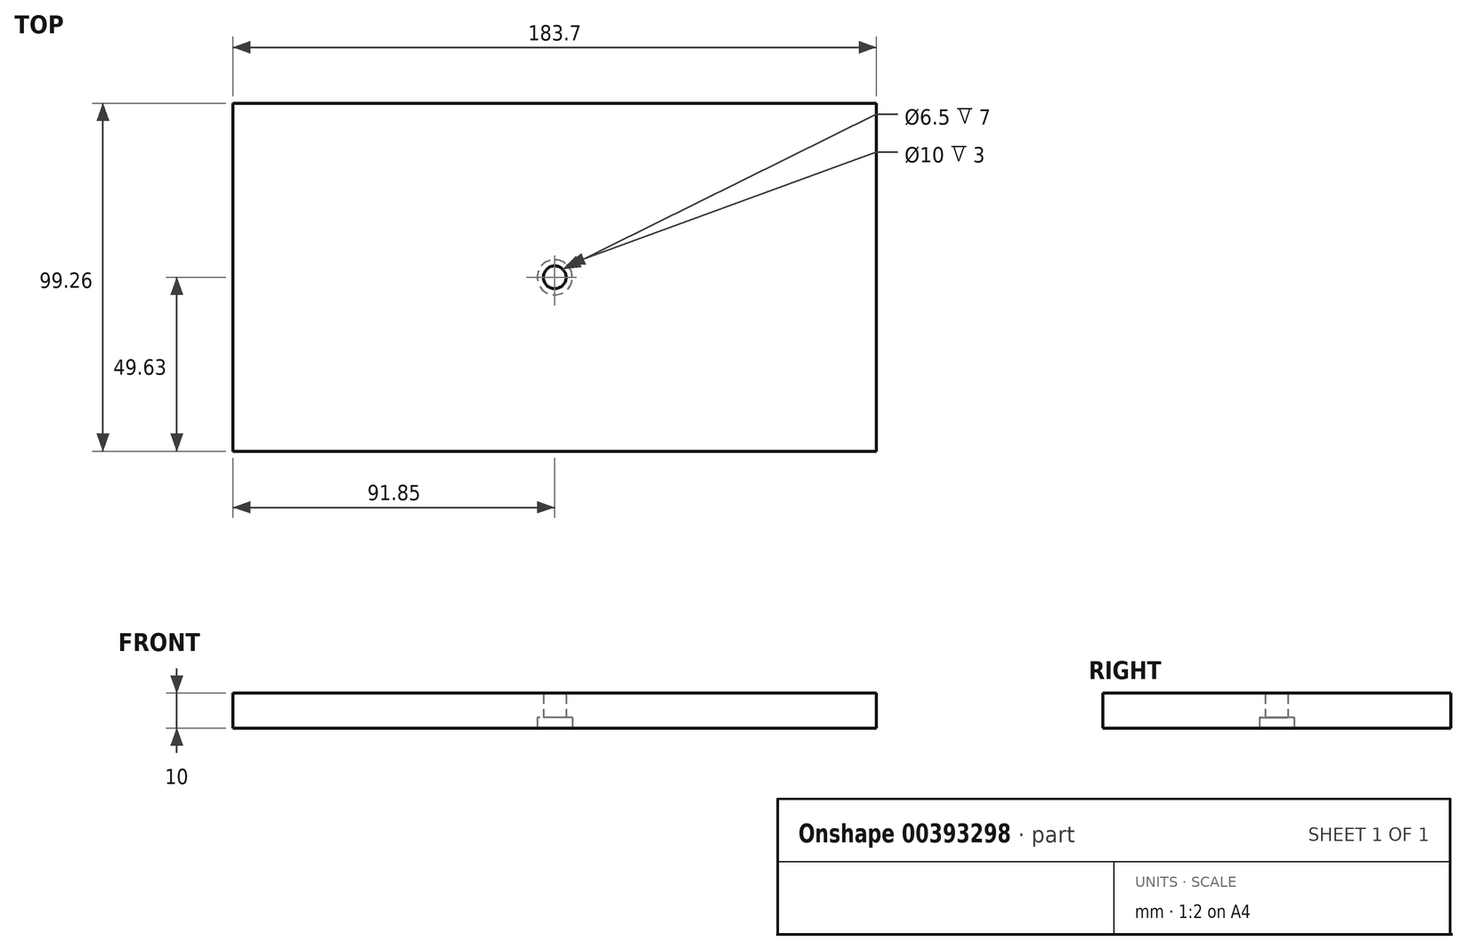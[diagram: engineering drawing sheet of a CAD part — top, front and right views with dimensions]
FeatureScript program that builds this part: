
annotation { "Feature Type Name" : "Feature", "Feature Type Description" : "" }
export const myFeature = defineFeature(function(context is Context, id is Id, definition is map)
    precondition{}
    {
        {
            var Q0;
            Q0=qCreatedBy(makeId("Top.planeOp"),FACE);
            var sketch = newSketch(context, id + "F0", { "sketchPlane" : qUnion([Q0])});
            skLineSegment(sketch, "E0.bottom", {"start": v(-91.85, 49.63) * mm, "end": v(91.85, 49.63) * mm});
            skLineSegment(sketch, "E0.top", {"start": v(-91.85, -49.63) * mm, "end": v(91.85, -49.63) * mm});
            skLineSegment(sketch, "E0.left", {"start": v(-91.85, 49.63) * mm, "end": v(-91.85, -49.63) * mm});
            skLineSegment(sketch, "E0.right", {"start": v(91.85, 49.63) * mm, "end": v(91.85, -49.63) * mm});
            skPoint(sketch, "E0.middle", {"position": v(0, 0) * mm});
            skCircle(sketch, "E1", {"center": v(0, 0) * mm, "radius": 3.25 * mm});
            skSolve(sketch);
        }
        {
            var Q0;
            Q0=makeQuery(id+"F0.imprint","IMPRINT",FACE,{"disambiguationData":[TD([[makeQuery(id+"F0.imprint","IMPRINT",EDGE,{"derivedFrom":sQuery(id+"F0.wireOp",EDGE,"E0.bottom")}),-1.0]])]});
            extrude(context, id + "F1", {"entities" : qUnion([Q0]), "depth" : 10 * mm, "offsetDistance" : 25 * mm});
        }
        {
            var Q0;
            Q0=makeQuery(id+"F0.imprint","IMPRINT",FACE,{"disambiguationData":[TD([[makeQuery(id+"F0.imprint","IMPRINT",EDGE,{"derivedFrom":sQuery(id+"F0.wireOp",EDGE,"E0.bottom")}),-1.0]])]});
            var sketch = newSketch(context, id + "F2", { "sketchPlane" : qUnion([Q0])});
            skCircle(sketch, "E2", {"center": v(0, 0) * mm, "radius": 5 * mm});
            skLineSegment(sketch, "E3", {"start": v(0, 16) * mm, "end": v(-5, 16) * mm});
            skLineSegment(sketch, "E4", {"start": v(-5, 16) * mm, "end": v(-5, 0) * mm});
            skLineSegment(sketch, "E5.MirrorCS", {"start": v(0, 16) * mm, "end": v(5, 16) * mm});
            skLineSegment(sketch, "E6.MirrorCS", {"start": v(5, 16) * mm, "end": v(5, 0) * mm});
            skSolve(sketch);
        }
        {
            var Q0;
            Q0=makeQuery(id+"F2.imprint","IMPRINT",FACE,{"disambiguationData":[TD([[makeQuery(id+"F2.imprint","IMPRINT",EDGE,{"derivedFrom":makeQuery(id+"F0.imprint","IMPRINT",EDGE,{"derivedFrom":sQuery(id+"F0.wireOp",EDGE,"E1")})}),-1.0]])]});
            extrude(context, id + "F3", {"entities" : qUnion([Q0]), "operationType" : NewBodyOperationType.REMOVE, "depth" : 3 * mm, "offsetDistance" : 25 * mm});
        }
    });
